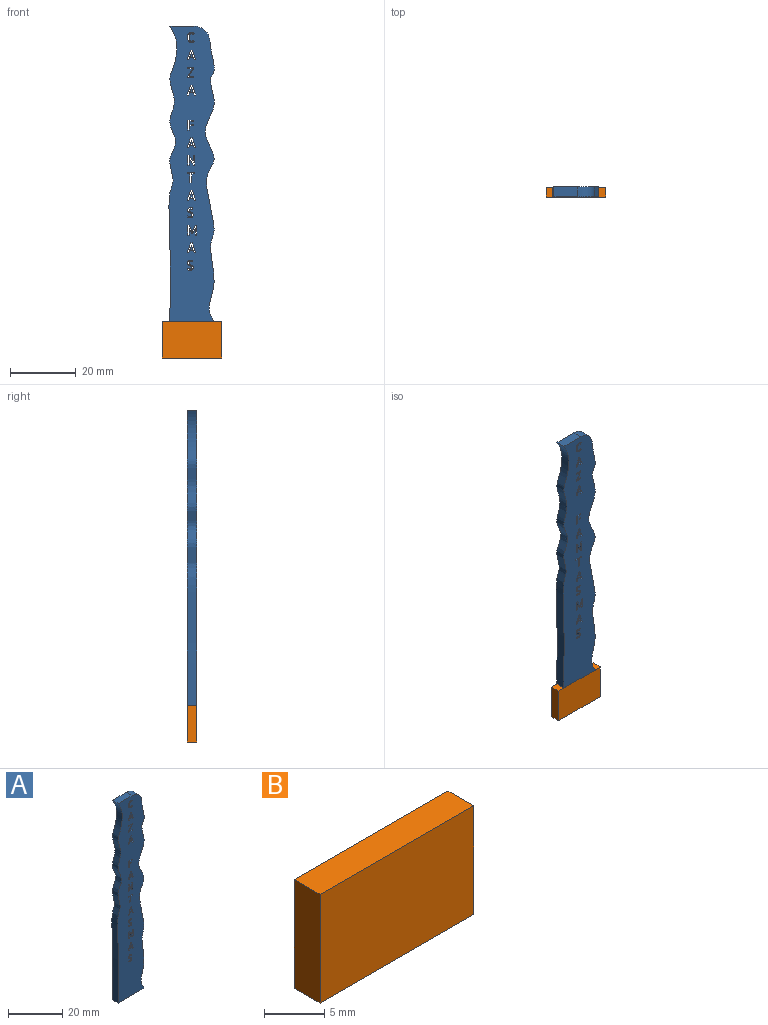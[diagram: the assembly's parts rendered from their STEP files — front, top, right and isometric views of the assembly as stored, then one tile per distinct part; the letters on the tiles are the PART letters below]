
ASSEMBLY  parts=2 mates=1
PART A: 250 faces, bbox 14.4x3x90 mm
  f0: plane 3x0.34mm, normal (-0.66,0,0.75), area 1.4mm2, adj f1,f246,f247,f248
  f1: extruded ~3x0.2mm, area 0.8mm2, adj f0,f2,f247,f248
  f2: extruded ~3x0.23mm, area 0.7mm2, adj f1,f3,f247,f248
  f3: plane 3x0.4mm, normal (1,0,0), area 1.2mm2, adj f2,f246,f247,f248
  f4: plane 3x0.4mm, normal (1,0,0), area 1.2mm2, adj f5,f216,f247,f248
  f5: extruded ~3x0.23mm, area 0.7mm2, adj f4,f6,f247,f248
  f6: extruded ~3x0.2mm, area 0.8mm2, adj f5,f7,f247,f248
  f7: plane 3x0.34mm, normal (-0.66,0,-0.75), area 1.3mm2, adj f6,f8,f247,f248
  f8: extruded ~3x0.35mm, area 1.3mm2, adj f7,f216,f247,f248
  f9: extruded ~3x0.64mm, area 1.9mm2, adj f10,f217,f247,f248
  f10: extruded ~3x0.64mm, area 1.9mm2, adj f9,f11,f247,f248
  f11: extruded ~3x0.47mm, area 1.6mm2, adj f10,f12,f247,f248
  f12: extruded ~3x0.36mm, area 1.4mm2, adj f11,f13,f247,f248
  f13: extruded ~3x0.46mm, area 1.4mm2, adj f12,f14,f247,f248
  f14: plane 3x0.41mm, normal (-1,0,0), area 1.2mm2, adj f13,f15,f247,f248
  f15: extruded ~3x0.25mm, area 0.8mm2, adj f14,f16,f247,f248
  f16: extruded ~3x0.21mm, area 0.9mm2, adj f15,f17,f247,f248
  f17: extruded ~3x0.34mm, area 1.1mm2, adj f16,f18,f247,f248
  f18: extruded ~3x0.49mm, area 1.5mm2, adj f17,f19,f247,f248
  f19: extruded ~3x0.49mm, area 1.5mm2, adj f18,f20,f247,f248
  f20: extruded ~3x0.34mm, area 1.1mm2, adj f19,f21,f247,f248
  f21: extruded ~3x0.21mm, area 0.9mm2, adj f20,f22,f247,f248
  f22: extruded ~3x0.25mm, area 0.8mm2, adj f21,f23,f247,f248
  f23: plane 3x0.4mm, normal (-1,0,0), area 1.2mm2, adj f22,f24,f247,f248
  f24: extruded ~3x0.46mm, area 1.4mm2, adj f23,f25,f247,f248
  f25: extruded ~3x0.36mm, area 1.4mm2, adj f24,f217,f247,f248
  f26: plane 3x2.99mm, normal (-0.94,0,-0.33), area 9.5mm2, adj f27,f218,f247,f248
  f27: plane 3x0.5mm, normal (0,0,1), area 1.5mm2, adj f26,f28,f247,f248
  f28: plane 3x2.25mm, normal (0.95,0,0.33), area 7.1mm2, adj f27,f29,f247,f248
  f29: plane 3x2.25mm, normal (-0.94,0,0.33), area 7.1mm2, adj f28,f30,f247,f248
  f30: plane 3x0.51mm, normal (0,0,1), area 1.5mm2, adj f29,f31,f247,f248
  f31: plane 3x2.99mm, normal (0.94,0,-0.33), area 9.5mm2, adj f30,f218,f247,f248
  f32: plane 3x0.55mm, normal (0,0,-1), area 1.6mm2, adj f33,f219,f247,f248
  f33: plane 3x0.33mm, normal (-0.94,0,-0.34), area 1.1mm2, adj f32,f34,f247,f248
  f34: plane 3x0.78mm, normal (0,0,1), area 2.3mm2, adj f33,f219,f247,f248
  f35: plane 3x1.99mm, normal (0,0,-1), area 6mm2, adj f36,f220,f247,f248
  f36: plane 3x0.39mm, normal (-1,0,0), area 1.2mm2, adj f35,f37,f247,f248
  f37: plane 3x2.14mm, normal (-0.83,0,0.55), area 7.7mm2, adj f36,f38,f247,f248
  f38: plane 3x0.08mm, normal (-0.62,0,0.78), area 0.3mm2, adj f37,f39,f247,f248
  f39: plane 3x1.51mm, normal (0,0,-1), area 4.5mm2, adj f38,f40,f247,f248
  f40: plane 3x0.39mm, normal (-1,0,0), area 1.2mm2, adj f39,f41,f247,f248
  f41: plane 3x1.99mm, normal (0,0,1), area 6mm2, adj f40,f42,f247,f248
  f42: plane 3x0.39mm, normal (1,0,0), area 1.2mm2, adj f41,f43,f247,f248
  f43: plane 3x2.14mm, normal (0.83,0,-0.55), area 7.7mm2, adj f42,f44,f247,f248
  f44: plane 3x0.09mm, normal (0.6,0,-0.8), area 0.3mm2, adj f43,f45,f247,f248
  f45: plane 3x1.51mm, normal (0,0,1), area 4.5mm2, adj f44,f220,f247,f248
  f46: plane 3x2.99mm, normal (-0.94,0,-0.33), area 9.5mm2, adj f47,f221,f247,f248
  f47: plane 3x0.5mm, normal (0,0,1), area 1.5mm2, adj f46,f48,f247,f248
  f48: plane 3x2.25mm, normal (0.95,0,0.33), area 7.1mm2, adj f47,f49,f247,f248
  f49: plane 3x2.25mm, normal (-0.94,0,0.33), area 7.1mm2, adj f48,f50,f247,f248
  f50: plane 3x0.51mm, normal (0,0,1), area 1.5mm2, adj f49,f51,f247,f248
  f51: plane 3x2.99mm, normal (0.94,0,-0.33), area 9.5mm2, adj f50,f221,f247,f248
  f52: plane 3x0.55mm, normal (0,0,-1), area 1.6mm2, adj f53,f222,f247,f248
  f53: plane 3x0.33mm, normal (-0.94,0,-0.34), area 1.1mm2, adj f52,f54,f247,f248
  f54: plane 3x0.78mm, normal (0,0,1), area 2.3mm2, adj f53,f222,f247,f248
  f55: plane 3x3mm, normal (1,0,0), area 9mm2, adj f56,f223,f247,f248
  f56: plane 3x0.5mm, normal (0,0,-1), area 1.5mm2, adj f55,f57,f247,f248
  f57: plane 3x3mm, normal (-1,0,0), area 9mm2, adj f56,f223,f247,f248
  f58: plane 3x0.33mm, normal (-1,0,0), area 1mm2, adj f59,f224,f247,f248
  f59: plane 3x1.09mm, normal (0,0,1), area 3.3mm2, adj f58,f60,f247,f248
  f60: plane 3x0.33mm, normal (1,0,0), area 1mm2, adj f59,f224,f247,f248
  f61: plane 3x1.21mm, normal (0,0,-1), area 3.6mm2, adj f62,f225,f247,f248
  f62: plane 3x0.37mm, normal (-1,0,0), area 1.1mm2, adj f61,f63,f247,f248
  f63: plane 3x1.21mm, normal (0,0,1), area 3.6mm2, adj f62,f225,f247,f248
  f64: plane 3x2.99mm, normal (-0.94,0,-0.33), area 9.5mm2, adj f65,f226,f247,f248
  f65: plane 3x0.5mm, normal (0,0,1), area 1.5mm2, adj f64,f66,f247,f248
  f66: plane 3x2.25mm, normal (0.95,0,0.33), area 7.1mm2, adj f65,f67,f247,f248
  f67: plane 3x2.25mm, normal (-0.94,0,0.33), area 7.1mm2, adj f66,f68,f247,f248
  f68: plane 3x0.51mm, normal (0,0,1), area 1.5mm2, adj f67,f69,f247,f248
  f69: plane 3x2.99mm, normal (0.94,0,-0.33), area 9.5mm2, adj f68,f226,f247,f248
  f70: plane 3x0.55mm, normal (0,0,-1), area 1.6mm2, adj f71,f227,f247,f248
  f71: plane 3x0.33mm, normal (-0.94,0,-0.34), area 1.1mm2, adj f70,f72,f247,f248
  f72: plane 3x0.78mm, normal (0,0,1), area 2.3mm2, adj f71,f227,f247,f248
  f73: plane 3x2.07mm, normal (1,0,0), area 6.2mm2, adj f74,f228,f247,f248
  f74: plane 3x0.5mm, normal (0,0,-1), area 1.5mm2, adj f73,f75,f247,f248
  f75: plane 3x3mm, normal (-1,0,0), area 9mm2, adj f74,f76,f247,f248
  f76: plane 3x0.5mm, normal (0,0,1), area 1.5mm2, adj f75,f77,f247,f248
  f77: plane 3x1.77mm, normal (0.87,0,0.49), area 6.1mm2, adj f76,f78,f247,f248
  f78: plane 3x0.94mm, normal (1,0,0), area 2.8mm2, adj f77,f228,f247,f248
  f79: plane 3x0.5mm, normal (0,0,1), area 1.5mm2, adj f80,f229,f247,f248
  f80: plane 3x3mm, normal (1,0,0), area 9mm2, adj f79,f81,f247,f248
  f81: plane 3x0.5mm, normal (0,0,-1), area 1.5mm2, adj f80,f229,f247,f248
  f82: plane 3x2.28mm, normal (0,0,-1), area 6.8mm2, adj f83,f230,f247,f248
  f83: plane 3x0.33mm, normal (-1,0,0), area 1mm2, adj f82,f84,f247,f248
  f84: plane 3x0.9mm, normal (0,0,1), area 2.7mm2, adj f83,f85,f247,f248
  f85: plane 3x2.67mm, normal (-1,0,0), area 8mm2, adj f84,f86,f247,f248
  f86: plane 3x0.49mm, normal (0,0,1), area 1.5mm2, adj f85,f87,f247,f248
  f87: plane 3x2.67mm, normal (1,0,0), area 8mm2, adj f86,f88,f247,f248
  f88: plane 3x0.9mm, normal (0,0,1), area 2.7mm2, adj f87,f230,f247,f248
  f89: plane 3x2.99mm, normal (-0.94,0,-0.33), area 9.5mm2, adj f90,f231,f247,f248
  f90: plane 3x0.5mm, normal (0,0,1), area 1.5mm2, adj f89,f91,f247,f248
  f91: plane 3x2.25mm, normal (0.95,0,0.33), area 7.1mm2, adj f90,f92,f247,f248
  f92: plane 3x2.25mm, normal (-0.94,0,0.33), area 7.1mm2, adj f91,f93,f247,f248
  f93: plane 3x0.51mm, normal (0,0,1), area 1.5mm2, adj f92,f94,f247,f248
  f94: plane 3x2.99mm, normal (0.94,0,-0.33), area 9.5mm2, adj f93,f231,f247,f248
  f95: plane 3x0.55mm, normal (0,0,-1), area 1.6mm2, adj f96,f232,f247,f248
  f96: plane 3x0.33mm, normal (-0.94,0,-0.34), area 1.1mm2, adj f95,f97,f247,f248
  f97: plane 3x0.78mm, normal (0,0,1), area 2.3mm2, adj f96,f232,f247,f248
  f98: extruded ~3x0.04mm, area 0.1mm2, adj f99,f233,f247,f248
  f99: extruded ~3x0.05mm, area 0.2mm2, adj f98,f100,f247,f248
  f100: extruded ~3x0.08mm, area 0.3mm2, adj f99,f101,f247,f248
  f101: extruded ~3x0.13mm, area 0.4mm2, adj f100,f102,f247,f248
  f102: extruded ~3x0.21mm, area 0.6mm2, adj f101,f103,f247,f248
  f103: plane 3x0.41mm, normal (1,0,0), area 1.2mm2, adj f102,f104,f247,f248
  f104: extruded ~3x0.36mm, area 1.1mm2, adj f103,f105,f247,f248
  f105: extruded ~3x0.3mm, area 1mm2, adj f104,f106,f247,f248
  f106: extruded ~3x0.12mm, area 0.4mm2, adj f105,f107,f247,f248
  f107: extruded ~3x0.12mm, area 0.4mm2, adj f106,f233,f247,f248
  f108: extruded ~3x0.32mm, area 1mm2, adj f109,f234,f247,f248
  f109: extruded ~3x0.32mm, area 1mm2, adj f108,f110,f247,f248
  f110: extruded ~3x0.25mm, area 0.9mm2, adj f109,f111,f247,f248
  f111: extruded ~3x0.24mm, area 0.9mm2, adj f110,f112,f247,f248
  f112: extruded ~3x0.3mm, area 0.9mm2, adj f111,f113,f247,f248
  f113: plane 3x0.43mm, normal (-1,0,0), area 1.3mm2, adj f112,f114,f247,f248
  f114: extruded ~3x0.22mm, area 0.8mm2, adj f113,f115,f247,f248
  f115: extruded ~3x0.23mm, area 0.7mm2, adj f114,f116,f247,f248
  f116: extruded ~3x0.26mm, area 0.8mm2, adj f115,f117,f247,f248
  f117: extruded ~3x0.22mm, area 0.8mm2, adj f116,f118,f247,f248
  f118: plane 3x0.46mm, normal (-1,0,0), area 1.4mm2, adj f117,f119,f247,f248
  f119: extruded ~3x0.27mm, area 0.9mm2, adj f118,f120,f247,f248
  f120: extruded ~3x0.24mm, area 0.9mm2, adj f119,f234,f247,f248
  f121: plane 3x0.35mm, normal (0.97,0,-0.24), area 1.1mm2, adj f122,f235,f247,f248
  f122: extruded ~3x0.14mm, area 0.5mm2, adj f121,f123,f247,f248
  f123: extruded ~3x0.18mm, area 0.6mm2, adj f122,f124,f247,f248
  f124: extruded ~3x0.19mm, area 0.6mm2, adj f123,f125,f247,f248
  f125: extruded ~3x0.18mm, area 0.5mm2, adj f124,f126,f247,f248
  f126: plane 3x0.01mm, normal (0,0,-1), area 0mm2, adj f125,f127,f247,f248
  f127: plane 3x0.39mm, normal (-1,0,0), area 1.2mm2, adj f126,f128,f247,f248
  f128: plane 3x0.01mm, normal (0,0,1), area 0mm2, adj f127,f129,f247,f248
  f129: extruded ~3x0.2mm, area 0.6mm2, adj f128,f130,f247,f248
  f130: extruded ~3x0.21mm, area 0.6mm2, adj f129,f131,f247,f248
  f131: extruded ~3x0.2mm, area 0.6mm2, adj f130,f235,f247,f248
  f132: plane 3x0.48mm, normal (1,0,0), area 1.4mm2, adj f133,f236,f247,f248
  f133: extruded ~3x0.27mm, area 0.9mm2, adj f132,f134,f247,f248
  f134: extruded ~3x0.25mm, area 0.9mm2, adj f133,f135,f247,f248
  f135: extruded ~3x0.24mm, area 0.9mm2, adj f134,f136,f247,f248
  f136: extruded ~3x0.35mm, area 1.1mm2, adj f135,f137,f247,f248
  f137: extruded ~3x0.29mm, area 0.9mm2, adj f136,f138,f247,f248
  f138: extruded ~3x0.25mm, area 0.9mm2, adj f137,f139,f247,f248
  f139: extruded ~3x0.25mm, area 0.9mm2, adj f138,f140,f247,f248
  f140: extruded ~3x0.33mm, area 1.1mm2, adj f139,f141,f247,f248
  f141: plane 3x0.39mm, normal (1,0,0), area 1.2mm2, adj f140,f142,f247,f248
  f142: extruded ~3x0.44mm, area 1.8mm2, adj f141,f143,f247,f248
  f143: extruded ~3x0.24mm, area 0.8mm2, adj f142,f236,f247,f248
  f144: plane 3x3mm, normal (1,0,0), area 9mm2, adj f145,f237,f247,f248
  f145: plane 3x0.5mm, normal (0,0,-1), area 1.5mm2, adj f144,f146,f247,f248
  f146: plane 3x1.85mm, normal (-0.92,0,-0.4), area 6.1mm2, adj f145,f147,f247,f248
  f147: plane 3x0.75mm, normal (-1,0,0), area 2.3mm2, adj f146,f148,f247,f248
  f148: plane 3x0.13mm, normal (0,0,1), area 0.4mm2, adj f147,f149,f247,f248
  f149: plane 3x1.67mm, normal (0.93,0,0.38), area 5.4mm2, adj f148,f150,f247,f248
  f150: plane 3x2.06mm, normal (-1,0,0), area 6.2mm2, adj f149,f237,f247,f248
  f151: plane 3x1.86mm, normal (0.92,0,-0.4), area 6.1mm2, adj f152,f238,f247,f248
  f152: plane 3x0.5mm, normal (0,0,-1), area 1.5mm2, adj f151,f153,f247,f248
  f153: plane 3x3mm, normal (-1,0,0), area 9mm2, adj f152,f154,f247,f248
  f154: plane 3x0.5mm, normal (0,0,1), area 1.5mm2, adj f153,f155,f247,f248
  f155: plane 3x2.06mm, normal (1,0,0), area 6.2mm2, adj f154,f156,f247,f248
  f156: plane 3x1.67mm, normal (-0.93,0,0.37), area 5.4mm2, adj f155,f157,f247,f248
  f157: plane 3x0.13mm, normal (0,0,1), area 0.4mm2, adj f156,f238,f247,f248
  f158: plane 3x2.99mm, normal (-0.94,0,-0.33), area 9.5mm2, adj f159,f239,f247,f248
  f159: plane 3x0.5mm, normal (0,0,1), area 1.5mm2, adj f158,f160,f247,f248
  f160: plane 3x2.25mm, normal (0.95,0,0.33), area 7.1mm2, adj f159,f161,f247,f248
  f161: plane 3x2.25mm, normal (-0.94,0,0.33), area 7.1mm2, adj f160,f162,f247,f248
  f162: plane 3x0.51mm, normal (0,0,1), area 1.5mm2, adj f161,f163,f247,f248
  f163: plane 3x2.99mm, normal (0.94,0,-0.33), area 9.5mm2, adj f162,f239,f247,f248
  f164: plane 3x0.55mm, normal (0,0,-1), area 1.6mm2, adj f165,f240,f247,f248
  f165: plane 3x0.33mm, normal (-0.94,0,-0.34), area 1.1mm2, adj f164,f166,f247,f248
  f166: plane 3x0.78mm, normal (0,0,1), area 2.3mm2, adj f165,f240,f247,f248
  f167: extruded ~3x0.04mm, area 0.1mm2, adj f168,f241,f247,f248
  f168: extruded ~3x0.05mm, area 0.2mm2, adj f167,f169,f247,f248
  f169: extruded ~3x0.08mm, area 0.3mm2, adj f168,f170,f247,f248
  f170: extruded ~3x0.13mm, area 0.4mm2, adj f169,f171,f247,f248
  f171: extruded ~3x0.21mm, area 0.6mm2, adj f170,f172,f247,f248
  f172: plane 3x0.41mm, normal (1,0,0), area 1.2mm2, adj f171,f173,f247,f248
  f173: extruded ~3x0.36mm, area 1.1mm2, adj f172,f174,f247,f248
  f174: extruded ~3x0.3mm, area 1mm2, adj f173,f175,f247,f248
  f175: extruded ~3x0.12mm, area 0.4mm2, adj f174,f176,f247,f248
  f176: extruded ~3x0.12mm, area 0.4mm2, adj f175,f241,f247,f248
  f177: extruded ~3x0.32mm, area 1mm2, adj f178,f242,f247,f248
  f178: extruded ~3x0.32mm, area 1mm2, adj f177,f179,f247,f248
  f179: extruded ~3x0.25mm, area 0.9mm2, adj f178,f180,f247,f248
  f180: extruded ~3x0.24mm, area 0.9mm2, adj f179,f181,f247,f248
  f181: extruded ~3x0.3mm, area 0.9mm2, adj f180,f182,f247,f248
  f182: plane 3x0.43mm, normal (-1,0,0), area 1.3mm2, adj f181,f183,f247,f248
  f183: extruded ~3x0.22mm, area 0.8mm2, adj f182,f184,f247,f248
  f184: extruded ~3x0.23mm, area 0.7mm2, adj f183,f185,f247,f248
  f185: extruded ~3x0.26mm, area 0.8mm2, adj f184,f186,f247,f248
  f186: extruded ~3x0.22mm, area 0.8mm2, adj f185,f187,f247,f248
  f187: plane 3x0.46mm, normal (-1,0,0), area 1.4mm2, adj f186,f188,f247,f248
  f188: extruded ~3x0.27mm, area 0.9mm2, adj f187,f189,f247,f248
  f189: extruded ~3x0.24mm, area 0.9mm2, adj f188,f242,f247,f248
  f190: plane 3x0.35mm, normal (0.97,0,-0.24), area 1.1mm2, adj f191,f243,f247,f248
  f191: extruded ~3x0.14mm, area 0.5mm2, adj f190,f192,f247,f248
  f192: extruded ~3x0.18mm, area 0.6mm2, adj f191,f193,f247,f248
  f193: extruded ~3x0.19mm, area 0.6mm2, adj f192,f194,f247,f248
  f194: extruded ~3x0.18mm, area 0.5mm2, adj f193,f195,f247,f248
  f195: plane 3x0.01mm, normal (0,0,-1), area 0mm2, adj f194,f196,f247,f248
  f196: plane 3x0.39mm, normal (-1,0,0), area 1.2mm2, adj f195,f197,f247,f248
  f197: plane 3x0.01mm, normal (0,0,1), area 0mm2, adj f196,f198,f247,f248
  f198: extruded ~3x0.2mm, area 0.6mm2, adj f197,f199,f247,f248
  f199: extruded ~3x0.21mm, area 0.6mm2, adj f198,f200,f247,f248
  f200: extruded ~3x0.2mm, area 0.6mm2, adj f199,f243,f247,f248
  f201: plane 3x0.48mm, normal (1,0,0), area 1.4mm2, adj f202,f244,f247,f248
  f202: extruded ~3x0.27mm, area 0.9mm2, adj f201,f203,f247,f248
  f203: extruded ~3x0.25mm, area 0.9mm2, adj f202,f204,f247,f248
  f204: extruded ~3x0.24mm, area 0.9mm2, adj f203,f205,f247,f248
  f205: extruded ~3x0.35mm, area 1.1mm2, adj f204,f206,f247,f248
  f206: extruded ~3x0.29mm, area 0.9mm2, adj f205,f207,f247,f248
  f207: extruded ~3x0.25mm, area 0.9mm2, adj f206,f208,f247,f248
  f208: extruded ~3x0.25mm, area 0.9mm2, adj f207,f209,f247,f248
  f209: extruded ~3x0.33mm, area 1.1mm2, adj f208,f210,f247,f248
  f210: plane 3x0.39mm, normal (1,0,0), area 1.2mm2, adj f209,f211,f247,f248
  f211: extruded ~3x0.44mm, area 1.8mm2, adj f210,f212,f247,f248
  f212: extruded ~3x0.24mm, area 0.8mm2, adj f211,f244,f247,f248
  f213: plane 7.22x3mm, normal (0,0,1), area 21.7mm2, adj f214,f247,f248,f249
  f214: extruded ~90x3mm, area 272.5mm2, adj f213,f215,f247,f248
  f215: plane 13.42x3mm, normal (0,0,-1), area 40.3mm2, adj f214,f245,f247,f248
  f216: extruded ~3x0.42mm, area 1.3mm2, adj f4,f8,f247,f248
  f217: extruded ~3x0.47mm, area 1.6mm2, adj f9,f25,f247,f248
  f218: plane 3x0.48mm, normal (0,0,-1), area 1.5mm2, adj f26,f31,f247,f248
  f219: plane 3x0.33mm, normal (0.95,0,-0.33), area 1mm2, adj f32,f34,f247,f248
  f220: plane 3x0.39mm, normal (1,0,0), area 1.2mm2, adj f35,f45,f247,f248
  f221: plane 3x0.48mm, normal (0,0,-1), area 1.5mm2, adj f46,f51,f247,f248
  f222: plane 3x0.33mm, normal (0.95,0,-0.33), area 1mm2, adj f52,f54,f247,f248
  f223: plane 3x0.5mm, normal (0,0,1), area 1.5mm2, adj f55,f57,f247,f248
  f224: plane 3x1.09mm, normal (0,0,-1), area 3.3mm2, adj f58,f60,f247,f248
  f225: plane 3x0.37mm, normal (1,0,0), area 1.1mm2, adj f61,f63,f247,f248
  f226: plane 3x0.48mm, normal (0,0,-1), area 1.5mm2, adj f64,f69,f247,f248
  f227: plane 3x0.33mm, normal (0.95,0,-0.33), area 1mm2, adj f70,f72,f247,f248
  f228: plane 3x1.78mm, normal (-0.87,0,-0.49), area 6.1mm2, adj f73,f78,f247,f248
  f229: plane 3x3mm, normal (-1,0,0), area 9mm2, adj f79,f81,f247,f248
  f230: plane 3x0.33mm, normal (1,0,0), area 1mm2, adj f82,f88,f247,f248
  f231: plane 3x0.48mm, normal (0,0,-1), area 1.5mm2, adj f89,f94,f247,f248
  f232: plane 3x0.33mm, normal (0.95,0,-0.33), area 1mm2, adj f95,f97,f247,f248
  f233: extruded ~3x0.09mm, area 0.3mm2, adj f98,f107,f247,f248
  f234: extruded ~3x0.24mm, area 0.9mm2, adj f108,f120,f247,f248
  f235: extruded ~3x0.17mm, area 0.6mm2, adj f121,f131,f247,f248
  f236: extruded ~3x0.24mm, area 0.9mm2, adj f132,f143,f247,f248
  f237: plane 3x0.5mm, normal (0,0,1), area 1.5mm2, adj f144,f150,f247,f248
  f238: plane 3x0.74mm, normal (1,0,0), area 2.2mm2, adj f151,f157,f247,f248
  f239: plane 3x0.48mm, normal (0,0,-1), area 1.5mm2, adj f158,f163,f247,f248
  f240: plane 3x0.33mm, normal (0.95,0,-0.33), area 1mm2, adj f164,f166,f247,f248
  f241: extruded ~3x0.09mm, area 0.3mm2, adj f167,f176,f247,f248
  f242: extruded ~3x0.24mm, area 0.9mm2, adj f177,f189,f247,f248
  f243: extruded ~3x0.17mm, area 0.6mm2, adj f190,f200,f247,f248
  f244: extruded ~3x0.24mm, area 0.9mm2, adj f201,f212,f247,f248
  f245: extruded ~85.09x3mm, area 264mm2, adj f215,f247,f248,f249
  f246: extruded ~3x0.77mm, area 2.5mm2, adj f0,f3,f247,f248
  f247: plane 90x14.42mm, normal (0,-1,0), area 1040.1mm2, adj f0,f1,f2,f3,f4,f5,f6,f7
  f248: plane 90x14.42mm, normal (0,1,0), area 1040.1mm2, adj f0,f1,f2,f3,f4,f5,f6,f7
  f249: cylinder r=5mm len=5mm, axis (0,1,0), area 23.3mm2, adj f213,f245,f247,f248
PART B: 6 faces, bbox 18x3x11 mm
  f0: plane 11.03x3mm, normal (1,0,0), area 33.1mm2, adj f1,f3,f4,f5
  f1: plane 18x3mm, normal (0,0,1), area 54mm2, adj f0,f2,f4,f5
  f2: plane 11.03x3mm, normal (-1,0,0), area 33.1mm2, adj f1,f3,f4,f5
  f3: plane 18x3mm, normal (0,0,-1), area 54mm2, adj f0,f2,f4,f5
  f4: plane 18x11.03mm, normal (0,1,0), area 198.5mm2, adj f0,f1,f2,f3
  f5: plane 18x11.03mm, normal (0,-1,0), area 198.5mm2, adj f0,f1,f2,f3
PLACE A at identity
PLACE B at identity fixed
MATE slider B.f1 <-> A.f215  axis (0,0,-1) through (1.71,-1.5,-82.6)mm
